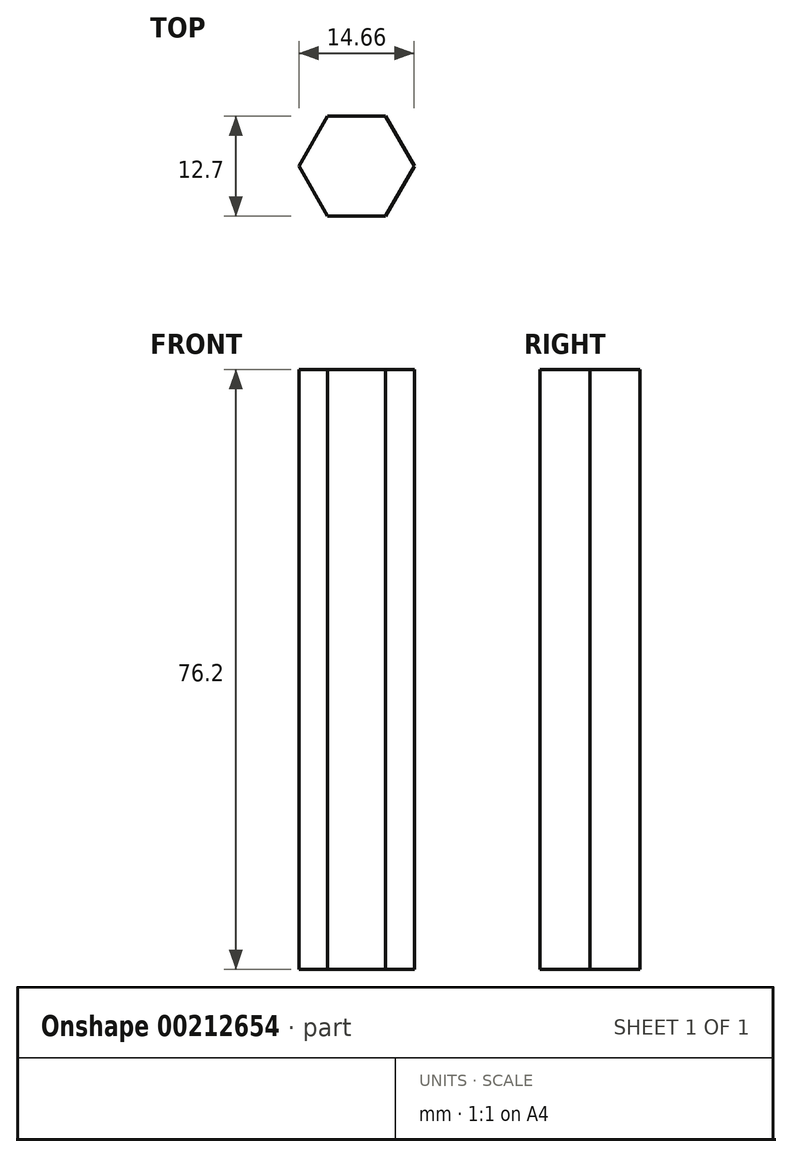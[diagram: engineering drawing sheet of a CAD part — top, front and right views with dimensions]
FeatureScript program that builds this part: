
annotation { "Feature Type Name" : "Feature", "Feature Type Description" : "" }
export const myFeature = defineFeature(function(context is Context, id is Id, definition is map)
    precondition{}
    {
        {
            var Q0;
            Q0=qCreatedBy(makeId("Top.planeOp"),FACE);
            var sketch = newSketch(context, id + "F0", { "sketchPlane" : qUnion([Q0])});
            skCircle(sketch, "E0.cCircle", {"center": v(0, 0) * mm, "radius": 6.35 * mm, "construction": true});
            skLineSegment(sketch, "E0.0", {"start": v(-3.67, 6.35) * mm, "end": v(3.67, 6.35) * mm});
            skLineSegment(sketch, "E0.1", {"start": v(3.67, 6.35) * mm, "end": v(7.33, 0) * mm});
            skLineSegment(sketch, "E0.2", {"start": v(7.33, 0) * mm, "end": v(3.67, -6.35) * mm});
            skLineSegment(sketch, "E0.3", {"start": v(3.67, -6.35) * mm, "end": v(-3.67, -6.35) * mm});
            skLineSegment(sketch, "E0.4", {"start": v(-3.67, -6.35) * mm, "end": v(-7.33, 0) * mm});
            skLineSegment(sketch, "E0.5", {"start": v(-7.33, 0) * mm, "end": v(-3.67, 6.35) * mm});
            skPoint(sketch, "E0.0.midPoint", {"position": v(0, 6.35) * mm});
            skSolve(sketch);
        }
        {
            var Q0;
            Q0=makeQuery(id+"F0.imprint","IMPRINT",FACE,{"disambiguationData":[TD([[makeQuery(id+"F0.imprint","IMPRINT",EDGE,{"derivedFrom":sQuery(id+"F0.wireOp",EDGE,"E0.0")}),-1.0]])]});
            var Q1;
            Q1=sQuery(id+"F0.wireOp",EDGE,"E0.4");
            extrude(context, id + "F1", {"entities" : qUnion([Q0]), "surfaceEntities" : qUnion([Q1]), "depth" : 76.2 * mm});
        }
    });
